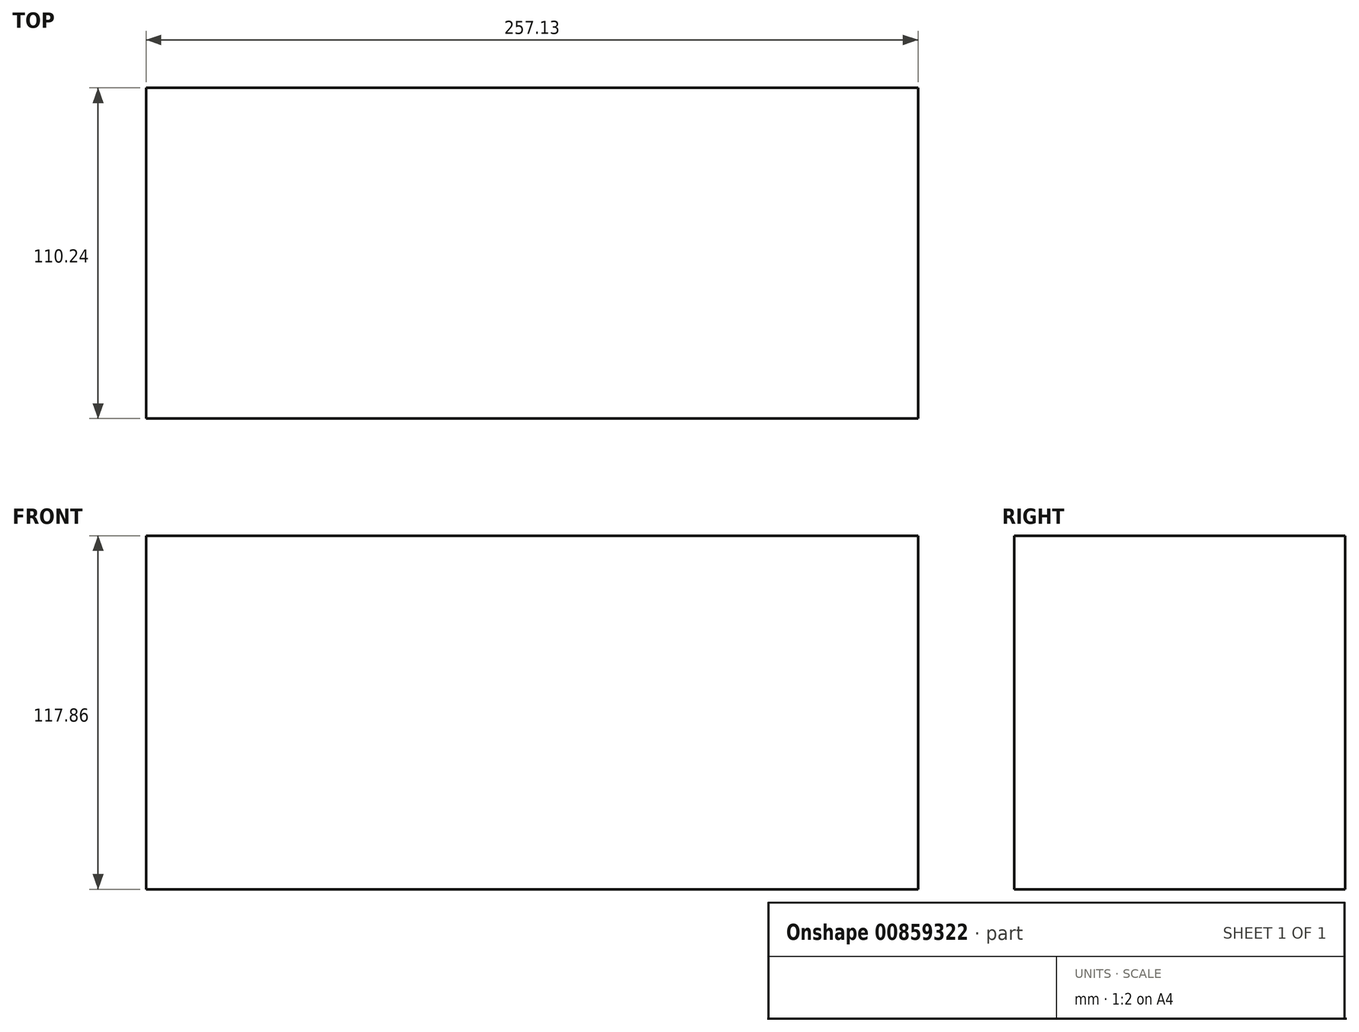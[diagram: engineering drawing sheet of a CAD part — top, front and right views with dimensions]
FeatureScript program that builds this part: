
annotation { "Feature Type Name" : "Feature", "Feature Type Description" : "" }
export const myFeature = defineFeature(function(context is Context, id is Id, definition is map)
    precondition{}
    {
        {
            var Q0;
            Q0=qCreatedBy(makeId("Front.planeOp"),FACE);
            var sketch = newSketch(context, id + "F0", { "sketchPlane" : qUnion([Q0])});
            skLineSegment(sketch, "E0.bottom", {"start": v(-120.35, -62.66) * mm, "end": v(136.78, -62.66) * mm});
            skLineSegment(sketch, "E0.top", {"start": v(-120.35, 55.2) * mm, "end": v(136.78, 55.2) * mm});
            skLineSegment(sketch, "E0.left", {"start": v(-120.35, -62.66) * mm, "end": v(-120.35, 55.2) * mm});
            skLineSegment(sketch, "E0.right", {"start": v(136.78, -62.66) * mm, "end": v(136.78, 55.2) * mm});
            skSolve(sketch);
        }
        {
            var Q0;
            Q0 = qSketchRegion(id + "F0", true);
            extrude(context, id + "F1", {"entities" : qUnion([Q0]), "depth" : 110.24 * mm, "offsetDistance" : 25.4 * mm});
        }
    });
